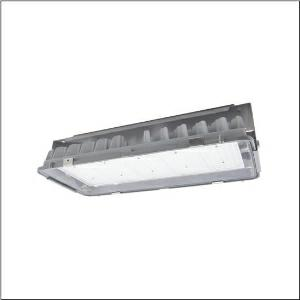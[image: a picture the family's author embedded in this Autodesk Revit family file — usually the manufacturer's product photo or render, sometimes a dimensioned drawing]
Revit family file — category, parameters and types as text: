
# Revit family: highbay_11xtreme_51hf82da4nma
name_source: partatom
category: Lighting Fixtures
units: mm (PartAtom-declared; Revit-internal decimal feet)

## family parameters
Cut with Voids When Loaded = No
Host = Face
Light Source = No
Part Type = Normal
Room Calculation Point = No
Round Connector Dimension = Use Diameter
Shared = No

## types (1)
- --- (1 x LED, 33700 lm, 187.7 W, 4000K)
    Apparent Load = 188 VA
    CIE Flux Codes = 84 96 100 100 100
    Color Rendering = 80
    Color Temperature = 4000K
    Default Elevation = 1800 mm
    Description = Highbay 11Xtreme, LED high bay luminaire, primary light control with lens, of PMMA, primary optical cover: cover, of toughened safety glass, light emission: direct distribution, primary light characteristic: symmetric, installation type: suspended mounting, surface-mounted, 1x LED module,for 1x LED, rated luminous flux: 33.700lm, luminous efficacy: 180lm/W, light colour: 840, colour temperature: 4000K, control gear: DALI 2, with cable H07RN-F 5x 1.5mm², mains connection: 220..240V, AC, 50/60Hz, cable length: 1,5m, rated input power: 188W, luminaire housing, of diecast aluminium, partly coated, silver, length: 595mm, width: 280mm, height: 195mm, protection rating (complete): IP66, insulation class (complete): insulation class I (protective earthing), certification: CE, ENEC, UKCA, protection symbol: D, ball protection: ball impact resistant according to DIN VDE 0710 part 13 (with chain suspension), impact resistance: IK08, permissible operating ambient temperature: -25..+45°C, reducing of maximum allowable ambient temperature of 5°C with ceiling mounting, packaging unit: 1 piece
    Height = 157 mm
    Lamp = 1 x LED
    Lamp Light Flux = 33700 lm
    Lamp Power = 187.7 W
    Lamp count = 1
    Length = 593 mm
    Luminous efficacy = 180 lm/W
    Manufacturer = Siteco
    ModVariant = No
    Model = 51HF82DA4NMA
    Mounting Place = Ceiling
    Mounting Type = Pendant
    Number of Poles = 1
    OnlyDefault = Yes
    Power Factor = 1
    Product Name = Highbay 11Xtreme
    Product group = LED high bay luminaire
    ProductGroupID = 903
    Protection Class = Protection class I
    Protection Degree = IP 66
    RLX_Detail_Level = 1
    RLX_Emergency_Light_Flux = 0 lm
    RLX_Emergency_Type = 0
    RLX_Emergency_Type_DB = No
    RlxData = <blob elided: 28381 chars, md5=44e88f32>
    Socket = socket
    Standby Power = 0 W
    System Light Flux = 33700 lm
    System Power = 188 W
    Type Comments = factory setting: luminous flux: 100 % | dim-lin: 254 | 1255 mA
    Type Image = l_1258342.jpg
    URL = http://relux.com
    VarID = @adj_080412
    Voltage = 0 V
    Weight = 0.00 kg
    Width = 568 mm

## geometry (parser evidence)
native form markers: Blend x4, Sweep x10
no freeform markers — native parametric forms only
